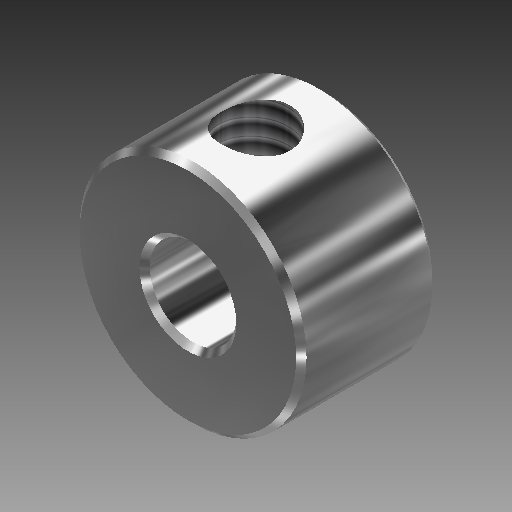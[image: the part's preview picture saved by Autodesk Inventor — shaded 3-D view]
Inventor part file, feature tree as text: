
AUTODESK INVENTOR PART (.ipt)
format: ipt  version: 2018 (Build 220112000, 112)  size: 169,472 bytes
history: native  units: in
note: dims shown in document units (in); Inventor stores cm internally (conversion verified against a paired STEP export)
features: sketch x3, chamfer x2, hole x2, extrude x1, plane x1
ambient origin geometry x8: Origin, YZ Plane, XZ Plane, XY Plane, X Axis, Y Axis, Z Axis, Center Point
bodies: Solid1 (feature_tree)
feature tree (9):
  extrude  "Extrusion1"  Depth=0.26in TaperAngle=0.0deg
  chamfer  "Chamfer1"  Distance=0.01in Angle=45.0deg
  hole  "Hole1"  [1 undecoded]
  plane  "Work Plane1"
  hole  "Hole2"  [1 undecoded]
  chamfer  "Chamfer2"  [1 undecoded]
  sketch  "Sketch1"  dims[d0=0.433in d1=0.26in d2=0.0in d3=0.01in d4=0.125in d5=45.0deg]
  sketch  "Sketch2"  dims[d6=0.165in d7=0.75in d8=0.375in d9=0.25in d10=0.5635in d11=1.0in d12=0.8108in]
  sketch  "Sketch3"  dims[d13=0.13in d14=0.75in d15=0.375in d16=0.25in d17=0.5635in d18=1.0in d19=0.8108in d20=0.01in d21=0.125in d22=45.0deg]
note: 3 required parameter values undecoded (feature->parameter linkage not recoverable at this tier; creation-order binding heuristic only, values carry confidence <= 0.55)
